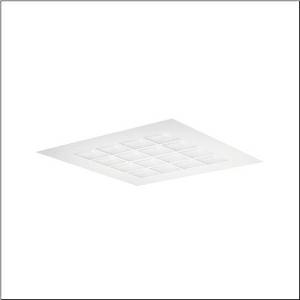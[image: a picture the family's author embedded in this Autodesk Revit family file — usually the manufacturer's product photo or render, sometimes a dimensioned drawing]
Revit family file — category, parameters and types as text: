
# Revit family: scriptus_r__11_5mz312ledzm00191xx_ec59
name_source: partatom
category: Lighting Fixtures
units: mm (PartAtom-declared; Revit-internal decimal feet)

## family parameters
Cut with Voids When Loaded = No
Host = Face
Light Source = No
Part Type = Normal
Room Calculation Point = No
Round Connector Dimension = Use Diameter
Shared = No

## types (1)
- Scriptus® 11 (1 x LED, 6400 lm, 37.5 W, 4000K)
    Apparent Load = 38 VA
    CIE Flux Codes = 80 95 99 100 100
    Color Rendering = 80
    Color Temperature = 4000K
    Default Elevation = 1800 mm
    Description = Scriptus® 11, office luminaire, primary optical cover: lenses, CAT 2 (L<= 3000cd/m²), light emission: direct distribution, primary light characteristic: symmetric, installation type: lay-in mounting, LED, rated luminous flux: 6.400lm, light colour: 840, colour temperature: 4000K, control gear: DALI, with terminal, 3+2-pole, max. 2.5mm², mains connection: 230V, AC, 50Hz, housing, of sheet steel, galvanised, traffic white (RAL 9016), module: M625, length: 621mm, width: 621mm, height: 68mm, protection rating (complete): IP20, insulation class (complete): insulation class I (protective earthing), certification: CE, impact resistance: IK02, permissible operating ambient temperature: 0..+35°C, standard: EN 50419, packaging unit: 1 piece
    Height = 80 mm  [stored 0.262467 ft]
    Lamp = 1 x LED
    Lamp Light Flux = 6400 lm
    Lamp Power = 37.5 W
    Lamp count = 1
    Length = 622 mm
    Luminous efficacy = 171 lm/W
    Manufacturer = Siteco
    ModVariant = No
    Model = 5MZ312LEDZM00191XX
    Mounting Place = Ceiling
    Mounting Type = Pendant
    Number of Poles = 1
    OnlyDefault = Yes
    Power Factor = 1
    Product Name = Scriptus® 11
    Product group = office luminaire | ceiling pendant
    ProductGroupID = 904
    Protection Class = Protection class I
    Protection Degree = IP 20
    RLX_Detail_Level = 1
    RLX_Emergency_Light_Flux = 0 lm
    RLX_Emergency_Type = 0
    RLX_Emergency_Type_DB = No
    RlxData = <blob elided: 19021 chars, md5=a9e85570>
    Socket = socket
    Standby Power = 0 W
    System Light Flux = 6400 lm
    System Power = 38 W
    Type Comments = Product without accessories
    Type Image = l_1006857.jpg
    URL = http://relux.com
    VarID = ---
    Voltage = 0 V
    Weight = 0.00 kg
    Width = 622 mm

note: [stored X ft] marks values corroborated as IEEE doubles in the binary element streams (Revit-internal decimal feet)

## geometry (parser evidence)
native form markers: Blend x4, Sweep x10
no freeform markers — native parametric forms only
